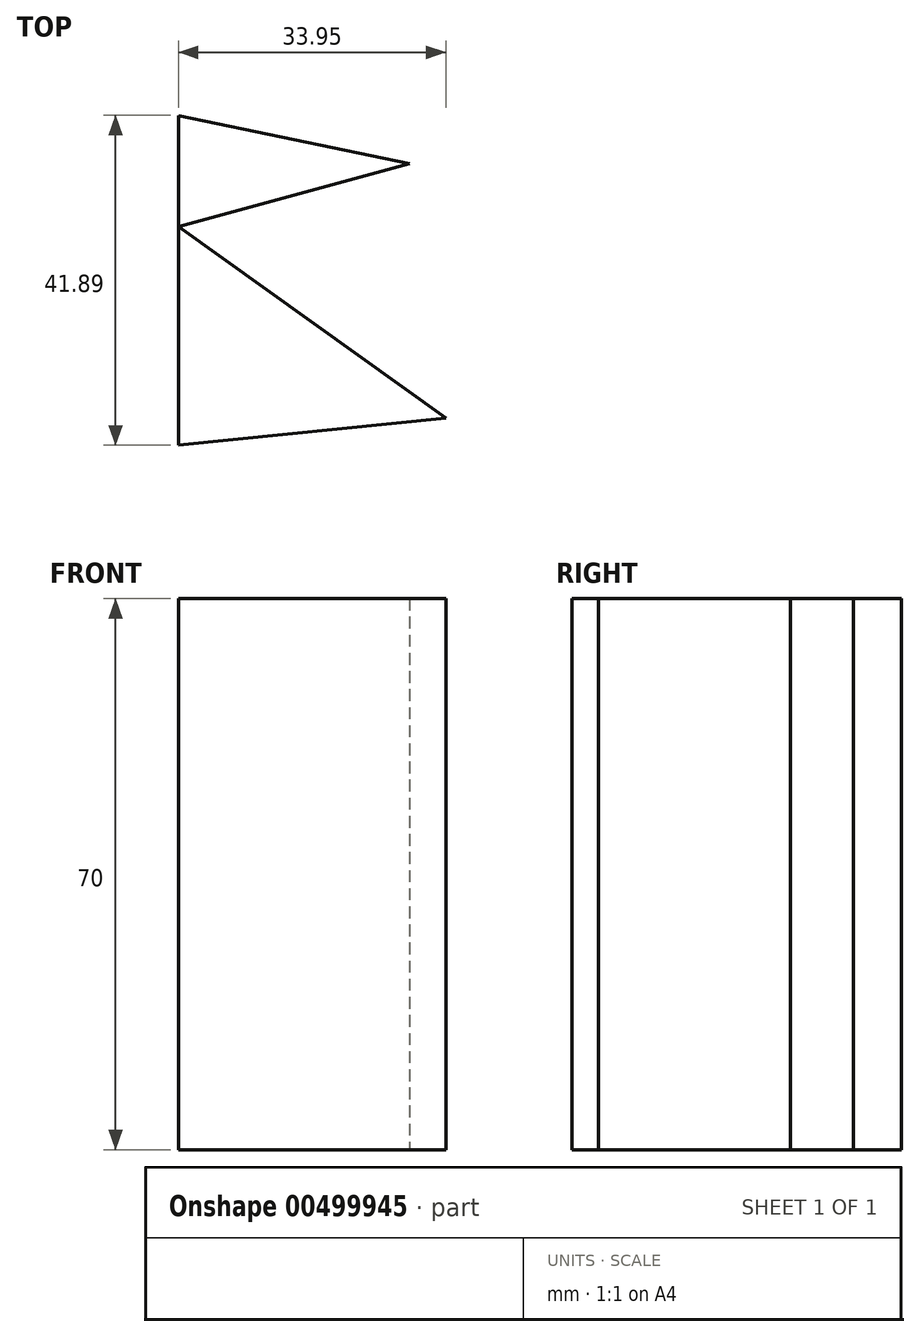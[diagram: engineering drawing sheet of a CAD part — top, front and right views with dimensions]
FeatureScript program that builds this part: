
annotation { "Feature Type Name" : "Feature", "Feature Type Description" : "" }
export const myFeature = defineFeature(function(context is Context, id is Id, definition is map)
    precondition{}
    {
        {
            var Q0;
            Q0=qCreatedBy(makeId("Top.planeOp"),FACE);
            var sketch = newSketch(context, id + "F0", { "sketchPlane" : qUnion([Q0])});
            skLineSegment(sketch, "E0", {"start": v(-51.35, 34.86) * mm, "end": v(-51.35, -7.03) * mm});
            skLineSegment(sketch, "E1", {"start": v(-51.35, -7.03) * mm, "end": v(-17.4, -3.62) * mm});
            skLineSegment(sketch, "E2", {"start": v(-17.4, -3.62) * mm, "end": v(-51.35, 20.73) * mm});
            skLineSegment(sketch, "E3", {"start": v(-51.35, 34.86) * mm, "end": v(-22.04, 28.7) * mm});
            skLineSegment(sketch, "E4", {"start": v(-22.04, 28.7) * mm, "end": v(-51.35, 20.73) * mm});
            skSolve(sketch);
        }
        {
            var Q0;
            {var subQ0=sQuery(id+"F0.wireOp",EDGE,"E1");Q0=makeQuery(id+"F0.imprint","IMPRINT",FACE,{"disambiguationData":[TD([[makeQuery(id+"F0.imprint","IMPRINT",EDGE,{"derivedFrom":subQ0}),1.0]])]});}
            var Q1;
            {var subQ0=sQuery(id+"F0.wireOp",EDGE,"E3");Q1=makeQuery(id+"F0.imprint","IMPRINT",FACE,{"disambiguationData":[TD([[makeQuery(id+"F0.imprint","IMPRINT",EDGE,{"derivedFrom":subQ0}),-1.0]])]});}
            extrude(context, id + "F1", {"entities" : qUnion([Q0, Q1]), "depth" : 70 * mm});
        }
    });
